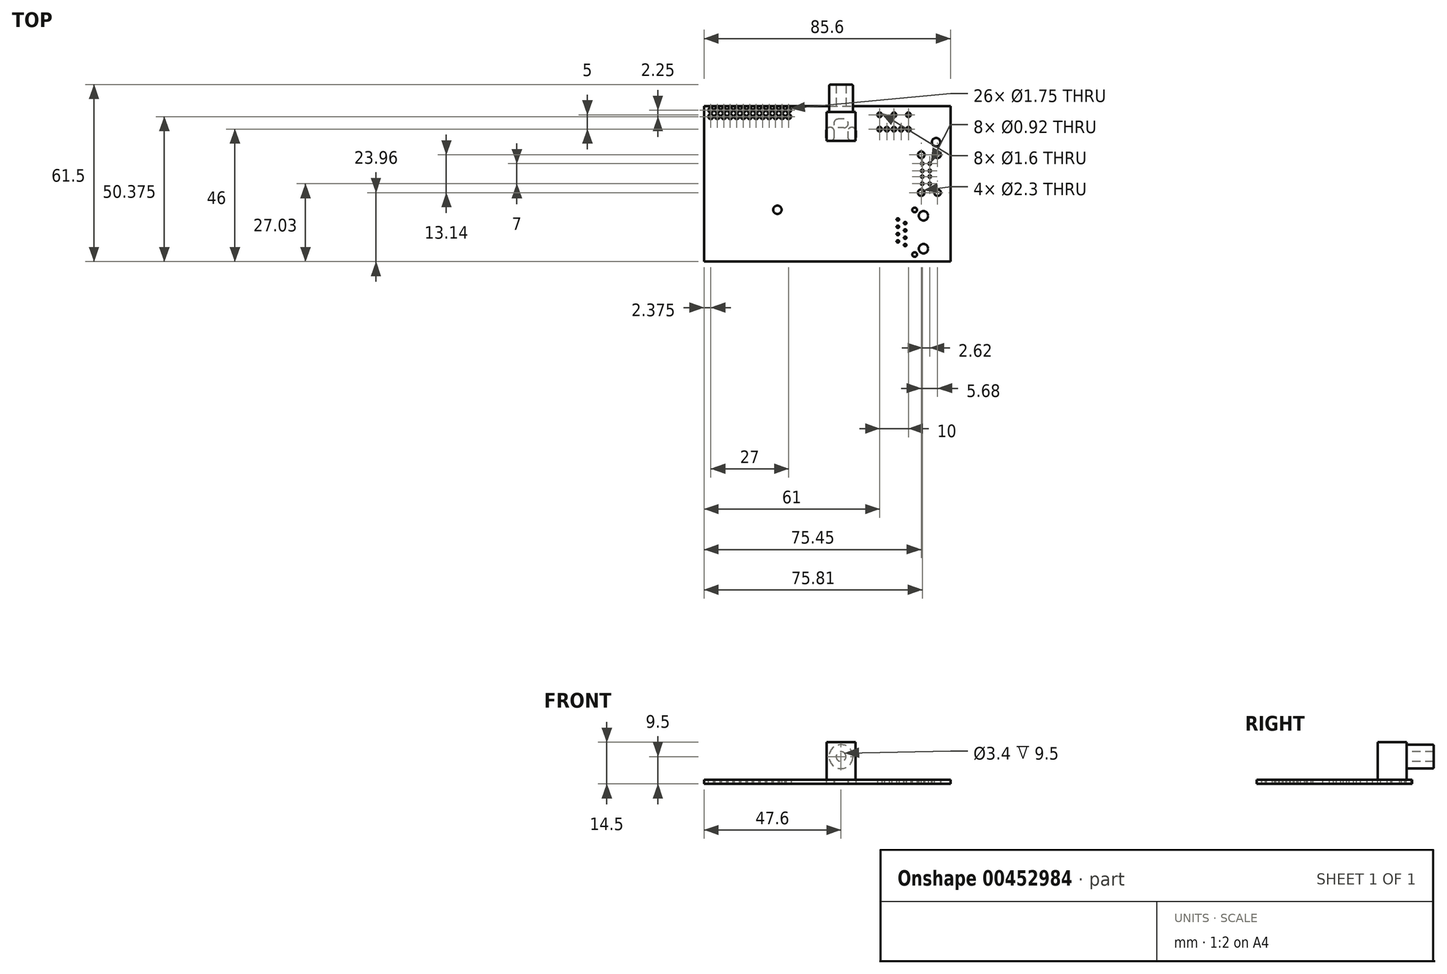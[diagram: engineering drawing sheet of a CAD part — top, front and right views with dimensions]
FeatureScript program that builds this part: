
annotation { "Feature Type Name" : "Feature", "Feature Type Description" : "" }
export const myFeature = defineFeature(function(context is Context, id is Id, definition is map)
    precondition{}
    {
        {
            var Q0;
            Q0=qCreatedBy(makeId("Top.planeOp"),FACE);
            var sketch = newSketch(context, id + "F0", { "sketchPlane" : qUnion([Q0])});
            skLineSegment(sketch, "E0.bottom", {"start": v(-42.8, 27) * mm, "end": v(42.8, 27) * mm});
            skLineSegment(sketch, "E0.top", {"start": v(-42.8, -27) * mm, "end": v(42.8, -27) * mm});
            skLineSegment(sketch, "E0.left", {"start": v(-42.8, 27) * mm, "end": v(-42.8, -27) * mm});
            skLineSegment(sketch, "E0.right", {"start": v(42.8, 27) * mm, "end": v(42.8, -27) * mm});
            skPoint(sketch, "E0.middle", {"position": v(0, 0) * mm});
            skLineSegment(sketch, "E1", {"start": v(33.42, -24.15) * mm, "end": v(33.42, -20.9) * mm, "construction": true});
            skCircle(sketch, "E2", {"center": v(33.42, -22.52) * mm, "radius": 1.62 * mm});
            skLineSegment(sketch, "E3", {"start": v(33.42, -22.52) * mm, "end": v(42.8, -22.52) * mm, "construction": true});
            skLineSegment(sketch, "E4", {"start": v(33.42, -22.52) * mm, "end": v(33.42, -11.1) * mm, "construction": true});
            skCircle(sketch, "E5", {"center": v(33.42, -11.1) * mm, "radius": 1.63 * mm});
            skLineSegment(sketch, "E6", {"start": v(33.42, -22.52) * mm, "end": v(30.37, -22.52) * mm, "construction": true});
            skLineSegment(sketch, "E7", {"start": v(30.37, -22.52) * mm, "end": v(30.37, -24.55) * mm, "construction": true});
            skCircle(sketch, "E8", {"center": v(30.37, -24.55) * mm, "radius": 0.82 * mm});
            skLineSegment(sketch, "E9", {"start": v(33.42, -11.1) * mm, "end": v(30.37, -11.1) * mm, "construction": true});
            skLineSegment(sketch, "E10", {"start": v(30.37, -11.1) * mm, "end": v(30.37, -9.06) * mm, "construction": true});
            skCircle(sketch, "E11", {"center": v(30.37, -9.06) * mm, "radius": 0.82 * mm});
            skPoint(sketch, "E12.endSnap0", {"position": v(31.9, -11.1) * mm});
            skPoint(sketch, "E13.endSnap0", {"position": v(31.9, -22.52) * mm});
            skLineSegment(sketch, "E14", {"start": v(33.42, -22.52) * mm, "end": v(27.07, -22.52) * mm, "construction": true});
            skLineSegment(sketch, "E15", {"start": v(33.42, -22.52) * mm, "end": v(33.42, -27) * mm, "construction": true});
            skLineSegment(sketch, "E16", {"start": v(27.07, -22.52) * mm, "end": v(27.07, -21.25) * mm, "construction": true});
            skCircle(sketch, "E17", {"center": v(27.07, -21.25) * mm, "radius": 0.45 * mm});
            skCircle(sketch, "E18.0.1.0", {"center": v(27.07, -18.71) * mm, "radius": 0.45 * mm});
            skCircle(sketch, "E18.0.2.0", {"center": v(27.07, -16.17) * mm, "radius": 0.45 * mm});
            skCircle(sketch, "E18.0.3.0", {"center": v(27.07, -13.63) * mm, "radius": 0.45 * mm});
            skLineSegment(sketch, "E18.direction2", {"start": v(27.07, -21.25) * mm, "end": v(27.07, -18.71) * mm, "construction": true});
            skLineSegment(sketch, "E19", {"start": v(27.07, -22.52) * mm, "end": v(24.53, -22.52) * mm, "construction": true});
            skLineSegment(sketch, "E20", {"start": v(24.53, -22.52) * mm, "end": v(24.53, -19.98) * mm, "construction": true});
            skCircle(sketch, "E21", {"center": v(24.53, -19.98) * mm, "radius": 0.45 * mm});
            skCircle(sketch, "E22.0.1.0", {"center": v(24.53, -17.44) * mm, "radius": 0.45 * mm});
            skCircle(sketch, "E22.0.2.0", {"center": v(24.53, -14.9) * mm, "radius": 0.45 * mm});
            skCircle(sketch, "E22.0.3.0", {"center": v(24.53, -12.36) * mm, "radius": 0.45 * mm});
            skLineSegment(sketch, "E22.direction2", {"start": v(24.53, -19.98) * mm, "end": v(24.53, -17.44) * mm, "construction": true});
            skLineSegment(sketch, "E23", {"start": v(32.65, 27) * mm, "end": v(32.65, 10.1) * mm, "construction": true});
            skCircle(sketch, "E24", {"center": v(32.65, 10.1) * mm, "radius": 1.15 * mm});
            skCircle(sketch, "E25.0.1.0", {"center": v(32.65, -3.04) * mm, "radius": 1.15 * mm});
            skCircle(sketch, "E25.1.0.0", {"center": v(38.33, 10.1) * mm, "radius": 1.15 * mm});
            skCircle(sketch, "E25.1.1.0", {"center": v(38.33, -3.04) * mm, "radius": 1.15 * mm});
            skLineSegment(sketch, "E25.direction1", {"start": v(32.65, 10.1) * mm, "end": v(38.33, 10.1) * mm, "construction": true});
            skLineSegment(sketch, "E25.direction2", {"start": v(32.65, 10.1) * mm, "end": v(32.65, -3.04) * mm, "construction": true});
            skLineSegment(sketch, "E26", {"start": v(32.65, 3.53) * mm, "end": v(33.01, 3.53) * mm, "construction": true});
            skPoint(sketch, "E26.endSnap0", {"position": v(32.65, 3.53) * mm});
            skLineSegment(sketch, "E27", {"start": v(33.01, 3.53) * mm, "end": v(33.01, 2.53) * mm, "construction": true});
            skCircle(sketch, "E28", {"center": v(33.01, 2.53) * mm, "radius": 0.46 * mm});
            skCircle(sketch, "E29.0.1.0", {"center": v(33.01, 4.53) * mm, "radius": 0.46 * mm});
            skCircle(sketch, "E29.1.0.0", {"center": v(35.63, 2.53) * mm, "radius": 0.46 * mm});
            skCircle(sketch, "E29.1.1.0", {"center": v(35.63, 4.53) * mm, "radius": 0.46 * mm});
            skLineSegment(sketch, "E29.direction1", {"start": v(33.01, 2.53) * mm, "end": v(35.63, 2.53) * mm, "construction": true});
            skLineSegment(sketch, "E29.direction2", {"start": v(33.01, 2.53) * mm, "end": v(33.01, 4.53) * mm, "construction": true});
            skLineSegment(sketch, "E30", {"start": v(33.01, 2.53) * mm, "end": v(33.01, 0.03) * mm, "construction": true});
            skCircle(sketch, "E31", {"center": v(33.01, 0.03) * mm, "radius": 0.46 * mm});
            skCircle(sketch, "E32.0.1.0", {"center": v(33.01, 7.03) * mm, "radius": 0.46 * mm});
            skCircle(sketch, "E32.1.0.0", {"center": v(35.63, 0.03) * mm, "radius": 0.46 * mm});
            skCircle(sketch, "E32.1.1.0", {"center": v(35.63, 7.03) * mm, "radius": 0.46 * mm});
            skLineSegment(sketch, "E32.direction1", {"start": v(33.01, 0.03) * mm, "end": v(35.63, 0.03) * mm, "construction": true});
            skLineSegment(sketch, "E33", {"start": v(42.8, 14.5) * mm, "end": v(37.8, 14.5) * mm, "construction": true});
            skLineSegment(sketch, "E34", {"start": v(37.8, 14.5) * mm, "end": v(37.8, 27) * mm, "construction": true});
            skCircle(sketch, "E35", {"center": v(37.8, 14.5) * mm, "radius": 1.45 * mm});
            skLineSegment(sketch, "E36", {"start": v(42.8, 24) * mm, "end": v(28.2, 24) * mm, "construction": true});
            skLineSegment(sketch, "E37", {"start": v(28.2, 24) * mm, "end": v(28.2, 27) * mm, "construction": true});
            skCircle(sketch, "E38", {"center": v(28.2, 24) * mm, "radius": 0.8 * mm});
            skLineSegment(sketch, "E39", {"start": v(28.2, 24) * mm, "end": v(18.2, 24) * mm, "construction": true});
            skCircle(sketch, "E40", {"center": v(18.2, 24) * mm, "radius": 0.8 * mm});
            skCircle(sketch, "E41", {"center": v(23.2, 24) * mm, "radius": 0.8 * mm});
            skLineSegment(sketch, "E42", {"start": v(28.2, 24) * mm, "end": v(28.2, 19) * mm, "construction": true});
            skCircle(sketch, "E43", {"center": v(28.2, 19) * mm, "radius": 0.8 * mm});
            skCircle(sketch, "E44.1.0.0", {"center": v(25.7, 19) * mm, "radius": 0.8 * mm});
            skCircle(sketch, "E44.2.0.0", {"center": v(23.2, 19) * mm, "radius": 0.8 * mm});
            skCircle(sketch, "E44.3.0.0", {"center": v(20.7, 19) * mm, "radius": 0.8 * mm});
            skCircle(sketch, "E44.4.0.0", {"center": v(18.2, 19) * mm, "radius": 0.8 * mm});
            skLineSegment(sketch, "E44.direction1", {"start": v(28.2, 19) * mm, "end": v(25.7, 19) * mm, "construction": true});
            skLineSegment(sketch, "E45", {"start": v(42.8, 21) * mm, "end": v(4.8, 21) * mm, "construction": true});
            skLineSegment(sketch, "E46", {"start": v(4.8, 21) * mm, "end": v(4.8, 27) * mm, "construction": true});
            skLineSegment(sketch, "E47.bottom", {"start": v(5.8, 22.5) * mm, "end": v(3.8, 22.5) * mm});
            skLineSegment(sketch, "E47.top", {"start": v(5.8, 19.5) * mm, "end": v(3.8, 19.5) * mm});
            skPoint(sketch, "E47.middle", {"position": v(4.8, 21) * mm});
            skArc(sketch, "E48", {"start": v(3.8, 22.5) * mm, "mid": v(2.3, 21) * mm, "end": v(3.8, 19.5) * mm});
            skArc(sketch, "E49", {"start": v(5.8, 19.5) * mm, "mid": v(7.3, 21) * mm, "end": v(5.8, 22.5) * mm});
            skLineSegment(sketch, "E50", {"start": v(4.8, 21) * mm, "end": v(4.8, 17.3) * mm, "construction": true});
            skLineSegment(sketch, "E51", {"start": v(4.8, 17.3) * mm, "end": v(1.05, 17.3) * mm, "construction": true});
            skLineSegment(sketch, "E52", {"start": v(4.8, 17.3) * mm, "end": v(8.55, 17.3) * mm, "construction": true});
            skLineSegment(sketch, "E53.left", {"start": v(2.42, 16.3) * mm, "end": v(2.42, 18.3) * mm});
            skLineSegment(sketch, "E53.right", {"start": v(-0.33, 16.3) * mm, "end": v(-0.33, 18.3) * mm});
            skPoint(sketch, "E53.middle", {"position": v(1.05, 17.3) * mm});
            skArc(sketch, "E54", {"start": v(2.42, 18.3) * mm, "mid": v(1.05, 19.67) * mm, "end": v(-0.33, 18.3) * mm});
            skArc(sketch, "E55", {"start": v(-0.33, 16.3) * mm, "mid": v(1.05, 14.92) * mm, "end": v(2.42, 16.3) * mm});
            skLineSegment(sketch, "E56.left", {"start": v(9.92, 18.3) * mm, "end": v(9.93, 16.3) * mm});
            skLineSegment(sketch, "E56.right", {"start": v(7.17, 18.3) * mm, "end": v(7.18, 16.3) * mm});
            skPoint(sketch, "E56.middle", {"position": v(8.55, 17.3) * mm});
            skArc(sketch, "E57", {"start": v(7.17, 16.3) * mm, "mid": v(8.55, 14.92) * mm, "end": v(9.92, 16.3) * mm});
            skArc(sketch, "E58", {"start": v(9.92, 18.3) * mm, "mid": v(8.55, 19.67) * mm, "end": v(7.17, 18.3) * mm});
            skLineSegment(sketch, "E59", {"start": v(-42.8, 25.62) * mm, "end": v(-40.43, 25.62) * mm, "construction": true});
            skLineSegment(sketch, "E60", {"start": v(-40.43, 25.62) * mm, "end": v(-40.43, 27) * mm, "construction": true});
            skCircle(sketch, "E61", {"center": v(-40.43, 25.62) * mm, "radius": 0.88 * mm});
            skCircle(sketch, "E62.0.1.0", {"center": v(-40.43, 23.37) * mm, "radius": 0.88 * mm});
            skCircle(sketch, "E62.1.0.0", {"center": v(-38.18, 25.62) * mm, "radius": 0.88 * mm});
            skCircle(sketch, "E62.1.1.0", {"center": v(-38.18, 23.37) * mm, "radius": 0.88 * mm});
            skCircle(sketch, "E62.2.0.0", {"center": v(-35.93, 25.62) * mm, "radius": 0.88 * mm});
            skCircle(sketch, "E62.2.1.0", {"center": v(-35.93, 23.37) * mm, "radius": 0.88 * mm});
            skCircle(sketch, "E62.3.0.0", {"center": v(-33.68, 25.62) * mm, "radius": 0.88 * mm});
            skCircle(sketch, "E62.3.1.0", {"center": v(-33.68, 23.37) * mm, "radius": 0.88 * mm});
            skCircle(sketch, "E62.4.0.0", {"center": v(-31.43, 25.62) * mm, "radius": 0.88 * mm});
            skCircle(sketch, "E62.4.1.0", {"center": v(-31.43, 23.37) * mm, "radius": 0.88 * mm});
            skCircle(sketch, "E62.5.0.0", {"center": v(-29.18, 25.62) * mm, "radius": 0.88 * mm});
            skCircle(sketch, "E62.5.1.0", {"center": v(-29.18, 23.37) * mm, "radius": 0.88 * mm});
            skCircle(sketch, "E62.6.0.0", {"center": v(-26.93, 25.62) * mm, "radius": 0.88 * mm});
            skCircle(sketch, "E62.6.1.0", {"center": v(-26.93, 23.37) * mm, "radius": 0.88 * mm});
            skCircle(sketch, "E62.7.0.0", {"center": v(-24.68, 25.62) * mm, "radius": 0.88 * mm});
            skCircle(sketch, "E62.7.1.0", {"center": v(-24.68, 23.37) * mm, "radius": 0.88 * mm});
            skCircle(sketch, "E62.8.0.0", {"center": v(-22.43, 25.62) * mm, "radius": 0.88 * mm});
            skCircle(sketch, "E62.8.1.0", {"center": v(-22.43, 23.37) * mm, "radius": 0.88 * mm});
            skCircle(sketch, "E62.9.0.0", {"center": v(-20.17, 25.62) * mm, "radius": 0.88 * mm});
            skCircle(sketch, "E62.9.1.0", {"center": v(-20.17, 23.37) * mm, "radius": 0.88 * mm});
            skCircle(sketch, "E62.10.0.0", {"center": v(-17.92, 25.62) * mm, "radius": 0.88 * mm});
            skCircle(sketch, "E62.10.1.0", {"center": v(-17.92, 23.37) * mm, "radius": 0.88 * mm});
            skCircle(sketch, "E62.11.0.0", {"center": v(-15.67, 25.62) * mm, "radius": 0.88 * mm});
            skCircle(sketch, "E62.11.1.0", {"center": v(-15.67, 23.37) * mm, "radius": 0.88 * mm});
            skCircle(sketch, "E62.12.0.0", {"center": v(-13.42, 25.62) * mm, "radius": 0.88 * mm});
            skCircle(sketch, "E62.12.1.0", {"center": v(-13.42, 23.37) * mm, "radius": 0.88 * mm});
            skLineSegment(sketch, "E62.direction1", {"start": v(-40.43, 25.62) * mm, "end": v(-38.18, 25.62) * mm, "construction": true});
            skLineSegment(sketch, "E62.direction2", {"start": v(-40.43, 25.62) * mm, "end": v(-40.43, 23.37) * mm, "construction": true});
            skLineSegment(sketch, "E63", {"start": v(-42.8, -9) * mm, "end": v(-17.3, -9) * mm, "construction": true});
            skLineSegment(sketch, "E64", {"start": v(-17.3, -9) * mm, "end": v(-17.3, -27) * mm, "construction": true});
            skCircle(sketch, "E65", {"center": v(-17.3, -9) * mm, "radius": 1.45 * mm});
            skSolve(sketch);
        }
        {
            var Q0;
            Q0=makeQuery(id+"F0.imprint","IMPRINT",FACE,{"disambiguationData":[TD([[makeQuery(id+"F0.imprint","IMPRINT",EDGE,{"derivedFrom":sQuery(id+"F0.wireOp",EDGE,"E0.bottom")}),-1.0]])]});
            extrude(context, id + "F1", {"entities" : qUnion([Q0]), "depth" : 1.5 * mm});
        }
        {
            var Q0;
            Q0=makeQuery(id+"F1.opExtrude","CAP_FACE",FACE,{"disambiguationData":[OSD([sQuery(id+"F0.wireOp",EDGE,"E0.bottom"),sQuery(id+"F0.wireOp",EDGE,"E0.top"),sQuery(id+"F0.wireOp",EDGE,"E0.left"),sQuery(id+"F0.wireOp",EDGE,"E0.right"),sQuery(id+"F0.wireOp",EDGE,"E2"),sQuery(id+"F0.wireOp",EDGE,"E5"),sQuery(id+"F0.wireOp",EDGE,"E8"),sQuery(id+"F0.wireOp",EDGE,"E11"),sQuery(id+"F0.wireOp",EDGE,"E17"),sQuery(id+"F0.wireOp",EDGE,"E18.0.1.0"),sQuery(id+"F0.wireOp",EDGE,"E18.0.2.0"),sQuery(id+"F0.wireOp",EDGE,"E18.0.3.0"),sQuery(id+"F0.wireOp",EDGE,"E21"),sQuery(id+"F0.wireOp",EDGE,"E22.0.1.0"),sQuery(id+"F0.wireOp",EDGE,"E22.0.2.0"),sQuery(id+"F0.wireOp",EDGE,"E22.0.3.0"),sQuery(id+"F0.wireOp",EDGE,"E24"),sQuery(id+"F0.wireOp",EDGE,"E25.0.1.0"),sQuery(id+"F0.wireOp",EDGE,"E25.1.0.0"),sQuery(id+"F0.wireOp",EDGE,"E25.1.1.0"),sQuery(id+"F0.wireOp",EDGE,"E28"),sQuery(id+"F0.wireOp",EDGE,"E29.0.1.0"),sQuery(id+"F0.wireOp",EDGE,"E29.1.0.0"),sQuery(id+"F0.wireOp",EDGE,"E29.1.1.0"),sQuery(id+"F0.wireOp",EDGE,"E31"),sQuery(id+"F0.wireOp",EDGE,"E32.0.1.0"),sQuery(id+"F0.wireOp",EDGE,"E32.1.0.0"),sQuery(id+"F0.wireOp",EDGE,"E32.1.1.0"),sQuery(id+"F0.wireOp",EDGE,"E35"),sQuery(id+"F0.wireOp",EDGE,"E38"),sQuery(id+"F0.wireOp",EDGE,"E40"),sQuery(id+"F0.wireOp",EDGE,"E41"),sQuery(id+"F0.wireOp",EDGE,"E43"),sQuery(id+"F0.wireOp",EDGE,"E44.1.0.0"),sQuery(id+"F0.wireOp",EDGE,"E44.2.0.0"),sQuery(id+"F0.wireOp",EDGE,"E44.3.0.0"),sQuery(id+"F0.wireOp",EDGE,"E44.4.0.0"),sQuery(id+"F0.wireOp",EDGE,"E47.bottom"),sQuery(id+"F0.wireOp",EDGE,"E47.top"),sQuery(id+"F0.wireOp",EDGE,"E48"),sQuery(id+"F0.wireOp",EDGE,"E49"),sQuery(id+"F0.wireOp",EDGE,"E53.left"),sQuery(id+"F0.wireOp",EDGE,"E53.right"),sQuery(id+"F0.wireOp",EDGE,"E54"),sQuery(id+"F0.wireOp",EDGE,"E55"),sQuery(id+"F0.wireOp",EDGE,"E56.left"),sQuery(id+"F0.wireOp",EDGE,"E56.right"),sQuery(id+"F0.wireOp",EDGE,"E57"),sQuery(id+"F0.wireOp",EDGE,"E58"),sQuery(id+"F0.wireOp",EDGE,"E61"),sQuery(id+"F0.wireOp",EDGE,"E62.0.1.0"),sQuery(id+"F0.wireOp",EDGE,"E62.1.0.0"),sQuery(id+"F0.wireOp",EDGE,"E62.1.1.0"),sQuery(id+"F0.wireOp",EDGE,"E62.2.0.0"),sQuery(id+"F0.wireOp",EDGE,"E62.2.1.0"),sQuery(id+"F0.wireOp",EDGE,"E62.3.0.0"),sQuery(id+"F0.wireOp",EDGE,"E62.3.1.0"),sQuery(id+"F0.wireOp",EDGE,"E62.4.0.0"),sQuery(id+"F0.wireOp",EDGE,"E62.4.1.0"),sQuery(id+"F0.wireOp",EDGE,"E62.5.0.0"),sQuery(id+"F0.wireOp",EDGE,"E62.5.1.0"),sQuery(id+"F0.wireOp",EDGE,"E62.6.0.0"),sQuery(id+"F0.wireOp",EDGE,"E62.6.1.0"),sQuery(id+"F0.wireOp",EDGE,"E62.7.0.0"),sQuery(id+"F0.wireOp",EDGE,"E62.7.1.0"),sQuery(id+"F0.wireOp",EDGE,"E62.8.0.0"),sQuery(id+"F0.wireOp",EDGE,"E62.8.1.0"),sQuery(id+"F0.wireOp",EDGE,"E62.9.0.0"),sQuery(id+"F0.wireOp",EDGE,"E62.9.1.0"),sQuery(id+"F0.wireOp",EDGE,"E62.10.0.0"),sQuery(id+"F0.wireOp",EDGE,"E62.10.1.0"),sQuery(id+"F0.wireOp",EDGE,"E62.11.0.0"),sQuery(id+"F0.wireOp",EDGE,"E62.11.1.0"),sQuery(id+"F0.wireOp",EDGE,"E62.12.0.0"),sQuery(id+"F0.wireOp",EDGE,"E62.12.1.0")])],"isStart":false});
            var sketch = newSketch(context, id + "F2", { "sketchPlane" : qUnion([Q0])});
            skPoint(sketch, "E66.endSnap0", {"position": v(4.8, 19.5) * mm});
            skLineSegment(sketch, "E67", {"start": v(4.8, 27) * mm, "end": v(4.8, 25) * mm, "construction": true});
            skLineSegment(sketch, "E68", {"start": v(4.8, 25) * mm, "end": v(4.8, 20) * mm, "construction": true});
            skLineSegment(sketch, "E69.bottom", {"start": v(-0.2, 15) * mm, "end": v(9.8, 15) * mm});
            skLineSegment(sketch, "E69.top", {"start": v(-0.2, 25) * mm, "end": v(9.8, 25) * mm});
            skLineSegment(sketch, "E69.left", {"start": v(-0.2, 15) * mm, "end": v(-0.2, 25) * mm});
            skLineSegment(sketch, "E69.right", {"start": v(9.8, 15) * mm, "end": v(9.8, 25) * mm});
            skPoint(sketch, "E69.middle", {"position": v(4.8, 20) * mm});
            skSolve(sketch);
        }
        {
            var Q0;
            {var subQ2=sQuery(id+"F2.wireOp",EDGE,"E69.top");Q0=makeQuery(id+"F2.imprint","IMPRINT",FACE,{"disambiguationData":[TD([[makeQuery(id+"F2.imprint","IMPRINT",EDGE,{"derivedFrom":subQ2}),-1.0]])]});}
            var Q1;
            Q1=makeQuery(id+"F2.imprint","IMPRINT",FACE,{"disambiguationData":[TD([[makeQuery(id+"F2.imprint","IMPRINT",EDGE,{"derivedFrom":makeQuery(id+"F1.opExtrude","CAP_EDGE",EDGE,{"disambiguationData":[OSD([sQuery(id+"F0.wireOp",EDGE,"E47.bottom")])],"isStart":false})}),1.0]])]});
            var Q2;
            {var subQ0=makeQuery(id+"F1.opExtrude","CAP_EDGE",EDGE,{"disambiguationData":[OSD([sQuery(id+"F0.wireOp",EDGE,"E56.right")])],"isStart":false});Q2=makeQuery(id+"F2.imprint","IMPRINT",FACE,{"disambiguationData":[TD([[makeQuery(id+"F2.imprint","IMPRINT",EDGE,{"derivedFrom":subQ0}),1.0]])]});}
            var Q3;
            {var subQ1=makeQuery(id+"F1.opExtrude","CAP_EDGE",EDGE,{"disambiguationData":[OSD([sQuery(id+"F0.wireOp",EDGE,"E53.left")])],"isStart":false});Q3=makeQuery(id+"F2.imprint","IMPRINT",FACE,{"disambiguationData":[TD([[makeQuery(id+"F2.imprint","IMPRINT",EDGE,{"derivedFrom":subQ1}),1.0]])]});}
            var Q4;
            {var subQ0=sQuery(id+"F2.wireOp",EDGE,"E69.left");var subQ1=sQuery(id+"F2.wireOp",EDGE,"E69.bottom");var subQ2=makeQuery(id+"F2.imprint","INTERSECT",VERTEX,{"derivedFrom":[subQ1,subQ0]});Q4=makeQuery(id+"F2.imprint","IMPRINT",FACE,{"disambiguationData":[TD([[makeQuery(id+"F2.imprint","IMPRINT",EDGE,{"disambiguationData":[TD([[subQ2,-1.0]])],"derivedFrom":subQ1}),1.0]])]});}
            var Q5;
            {var subQ0=sQuery(id+"F2.wireOp",EDGE,"E69.right");var subQ1=sQuery(id+"F2.wireOp",EDGE,"E69.bottom");var subQ2=makeQuery(id+"F2.imprint","INTERSECT",VERTEX,{"derivedFrom":[subQ1,subQ0]});Q5=makeQuery(id+"F2.imprint","IMPRINT",FACE,{"disambiguationData":[TD([[makeQuery(id+"F2.imprint","IMPRINT",EDGE,{"disambiguationData":[TD([[subQ2,1.0]])],"derivedFrom":subQ1}),1.0]])]});}
            var Q6;
            Q6=sQuery(id+"F2.wireOp",EDGE,"E69.left");
            var Q7;
            Q7=sQuery(id+"F2.wireOp",EDGE,"E69.top");
            var Q8;
            Q8=sQuery(id+"F2.wireOp",EDGE,"E69.right");
            var Q9;
            Q9=sQuery(id+"F2.wireOp",EDGE,"E69.bottom");
            extrude(context, id + "F3", {"entities" : qUnion([Q0, Q1, Q2, Q3, Q4, Q5]), "operationType" : NewBodyOperationType.ADD, "surfaceEntities" : qUnion([Q6, Q7, Q8, Q9]), "depth" : 13 * mm});
        }
        {
            var Q0;
            Q0=makeQuery(id+"F3.opExtrude","SWEPT_FACE",FACE,{"disambiguationData":[OSD([sQuery(id+"F2.wireOp",EDGE,"E69.top")])]});
            var sketch = newSketch(context, id + "F4", { "sketchPlane" : qUnion([Q0])});
            skLineSegment(sketch, "E70", {"start": v(-4.8, 1.5) * mm, "end": v(-4.8, 9.5) * mm, "construction": true});
            skCircle(sketch, "E71", {"center": v(-4.8, 9.5) * mm, "radius": 4.15 * mm});
            skCircle(sketch, "E72", {"center": v(-4.8, 9.5) * mm, "radius": 1.7 * mm});
            skSolve(sketch);
        }
        {
            var Q0;
            Q0=makeQuery(id+"F4.imprint","IMPRINT",FACE,{"disambiguationData":[TD([[makeQuery(id+"F4.imprint","IMPRINT",EDGE,{"derivedFrom":sQuery(id+"F4.wireOp",EDGE,"E71")}),1.0]])]});
            extrude(context, id + "F5", {"entities" : qUnion([Q0]), "operationType" : NewBodyOperationType.ADD, "depth" : 9.5 * mm});
        }
        {
            var Q0;
            Q0=makeQuery(id+"F5.opExtrude","CAP_EDGE",EDGE,{"disambiguationData":[OSD([sQuery(id+"F4.wireOp",EDGE,"E71")])],"isStart":false});
            fillet(context, id + "F6", {"entities" : qUnion([Q0]), "radius" : 0.5 * mm, "allowEdgeOverflow" : false});
        }
    });
